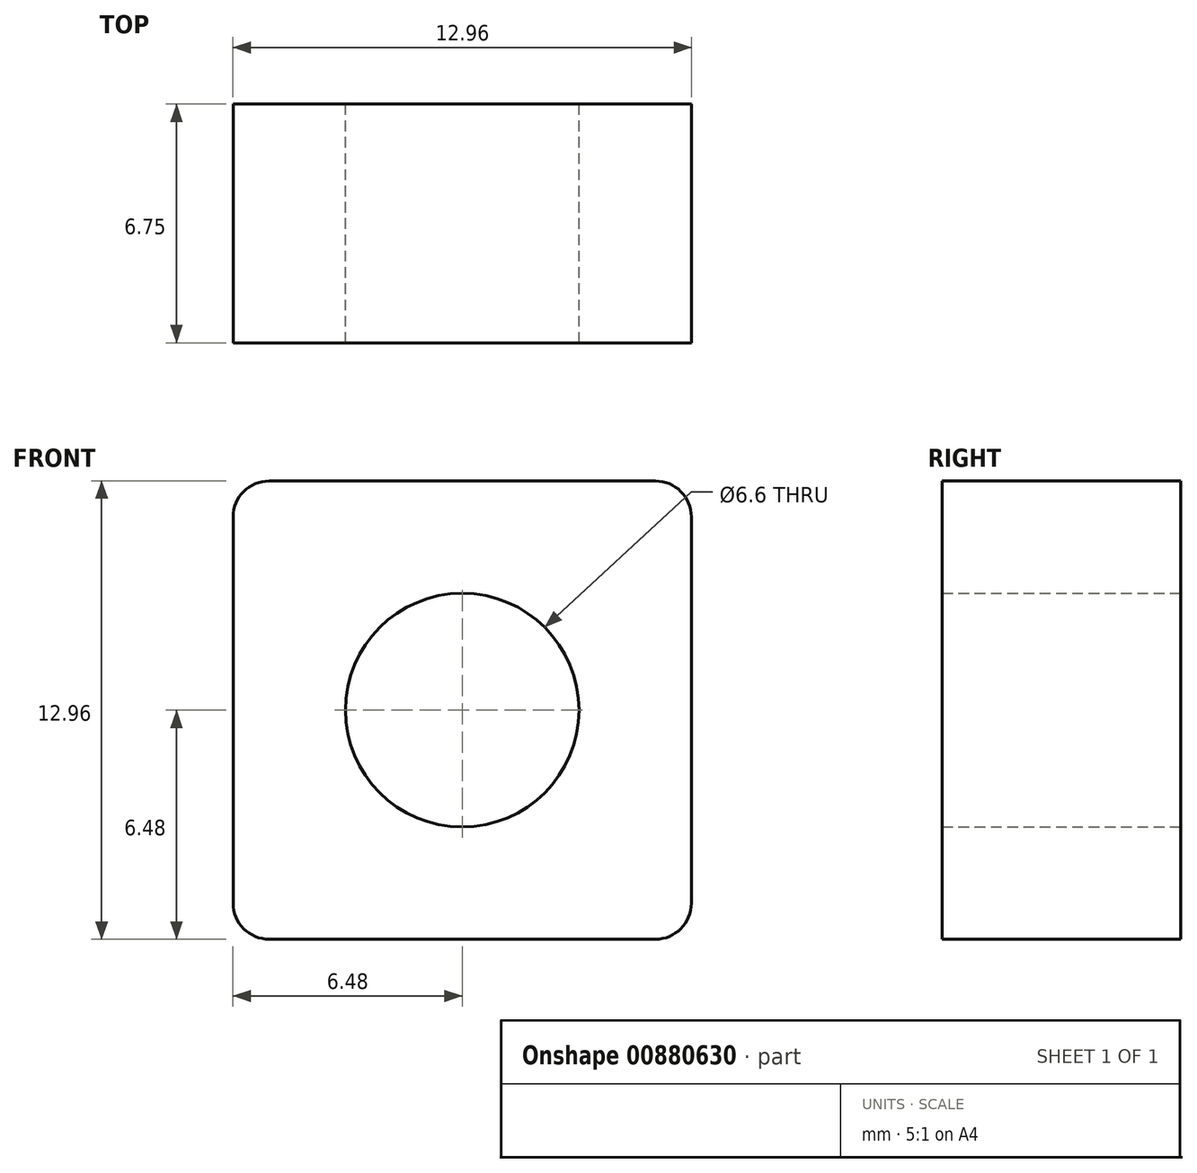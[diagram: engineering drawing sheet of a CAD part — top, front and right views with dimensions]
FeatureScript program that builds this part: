
annotation { "Feature Type Name" : "Feature", "Feature Type Description" : "" }
export const myFeature = defineFeature(function(context is Context, id is Id, definition is map)
    precondition{}
    {
        {
            var Q0;
            Q0=qCreatedBy(makeId("Front.planeOp"),FACE);
            var sketch = newSketch(context, id + "F0", { "sketchPlane" : qUnion([Q0])});
            skCircle(sketch, "E0", {"center": v(0, 0) * mm, "radius": 3.3 * mm});
            skLineSegment(sketch, "E1.bottom", {"start": v(-5.46, 6.48) * mm, "end": v(5.46, 6.48) * mm});
            skLineSegment(sketch, "E1.top", {"start": v(-5.46, -6.48) * mm, "end": v(5.46, -6.48) * mm});
            skLineSegment(sketch, "E1.left", {"start": v(-6.48, 5.46) * mm, "end": v(-6.48, -5.46) * mm});
            skLineSegment(sketch, "E1.right", {"start": v(6.48, 5.46) * mm, "end": v(6.48, -5.46) * mm});
            skCircle(sketch, "E2", {"center": v(0, 0) * mm, "radius": 6.48 * mm, "construction": true});
            skPoint(sketch, "E3.visualSharp", {"position": v(-6.48, -6.48) * mm});
            skArc(sketch, "E3.filletArc", {"start": v(-6.48, -5.46) * mm, "mid": v(-6.18, -6.18) * mm, "end": v(-5.46, -6.48) * mm});
            skPoint(sketch, "E4.visualSharp", {"position": v(6.48, -6.48) * mm});
            skArc(sketch, "E4.filletArc", {"start": v(5.46, -6.48) * mm, "mid": v(6.18, -6.18) * mm, "end": v(6.48, -5.46) * mm});
            skPoint(sketch, "E5.visualSharp", {"position": v(6.48, 6.48) * mm});
            skArc(sketch, "E5.filletArc", {"start": v(6.48, 5.46) * mm, "mid": v(6.18, 6.18) * mm, "end": v(5.46, 6.48) * mm});
            skPoint(sketch, "E6.visualSharp", {"position": v(-6.48, 6.48) * mm});
            skArc(sketch, "E6.filletArc", {"start": v(-5.46, 6.48) * mm, "mid": v(-6.18, 6.18) * mm, "end": v(-6.48, 5.46) * mm});
            skSolve(sketch);
        }
        {
            var Q0;
            Q0 = qSketchRegion(id + "F0", true);
            extrude(context, id + "F1", {"entities" : qUnion([Q0]), "depth" : 6.75 * mm, "offsetDistance" : 25.4 * mm});
        }
    });
